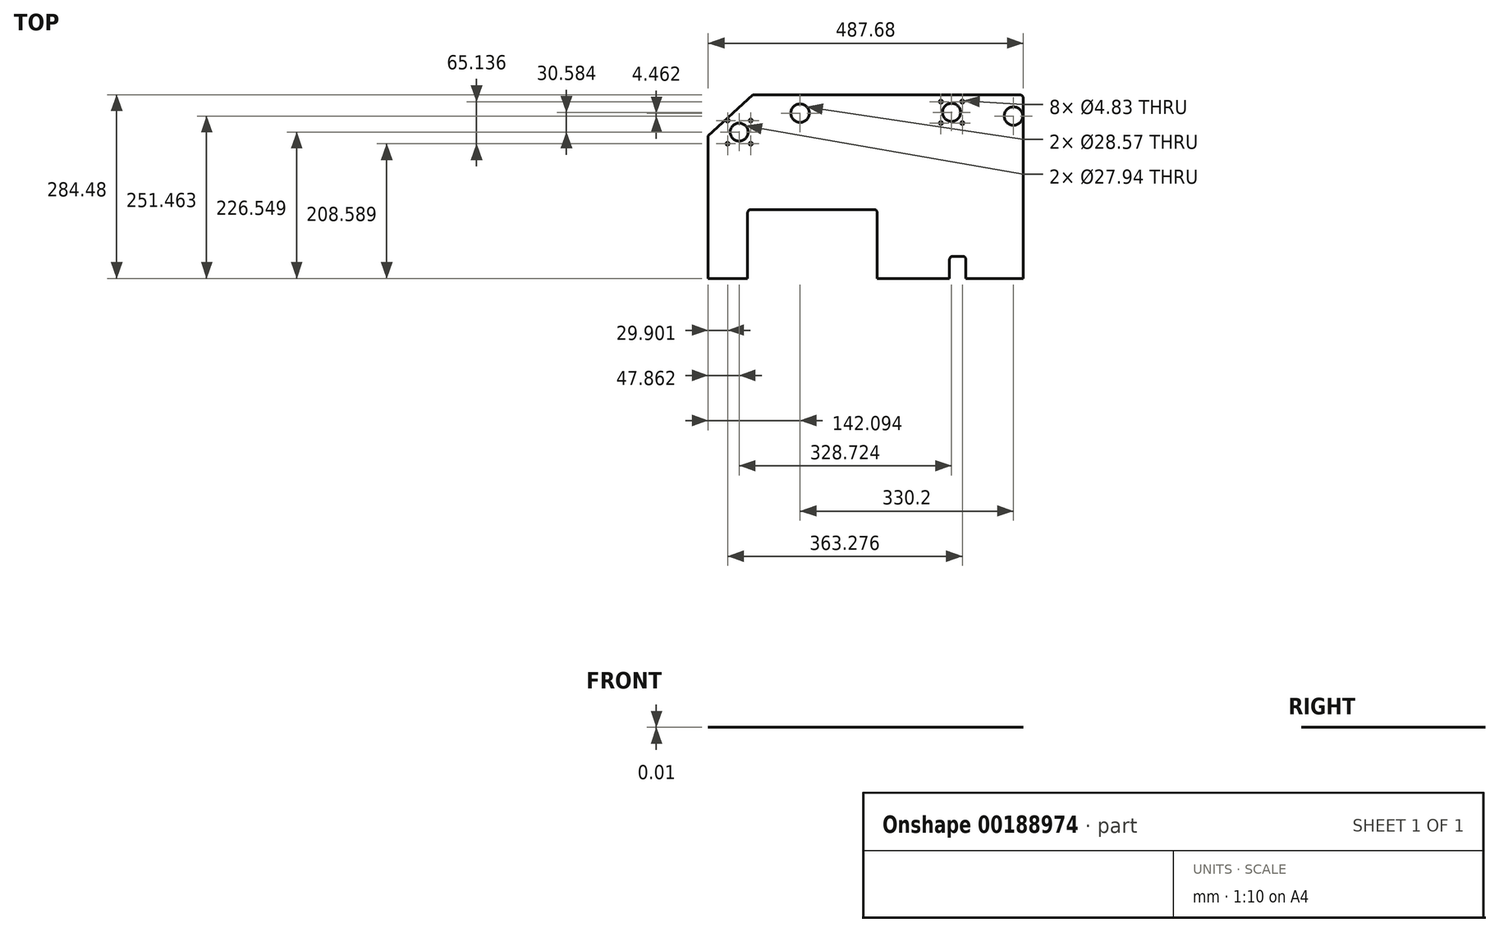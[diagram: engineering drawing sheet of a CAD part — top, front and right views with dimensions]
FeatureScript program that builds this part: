
annotation { "Feature Type Name" : "Feature", "Feature Type Description" : "" }
export const myFeature = defineFeature(function(context is Context, id is Id, definition is map)
    precondition{}
    {
        {
            var Q0;
            Q0=qCreatedBy(makeId("Top.planeOp"),FACE);
            var sketch = newSketch(context, id + "F0", { "sketchPlane" : qUnion([Q0])});
            skLineSegment(sketch, "E0.bottom", {"start": v(29.14, 37.07) * mm, "end": v(441.77, 37.07) * mm});
            skLineSegment(sketch, "E0.top", {"start": v(-39.56, -247.4) * mm, "end": v(21.4, -247.4) * mm});
            skLineSegment(sketch, "E0.left", {"start": v(-39.56, -26.6) * mm, "end": v(-39.56, -247.4) * mm});
            skLineSegment(sketch, "E0.right", {"start": v(448.12, 30.72) * mm, "end": v(448.12, -247.4) * mm});
            skLineSegment(sketch, "E1", {"start": v(-39.56, -26.6) * mm, "end": v(29.14, 37.07) * mm});
            skLineSegment(sketch, "E2.bottom", {"start": v(448.12, -247.4) * mm, "end": v(359.22, -247.4) * mm, "construction": true});
            skLineSegment(sketch, "E2.top", {"start": v(448.12, 37.07) * mm, "end": v(-39.56, 37.07) * mm, "construction": true});
            skLineSegment(sketch, "E2.left", {"start": v(448.12, -247.4) * mm, "end": v(448.12, 37.07) * mm, "construction": true});
            skLineSegment(sketch, "E2.right", {"start": v(-39.56, -247.4) * mm, "end": v(-39.56, 37.07) * mm, "construction": true});
            skCircle(sketch, "E3", {"center": v(432.73, 4.05) * mm, "radius": 14.29 * mm});
            skCircle(sketch, "E4", {"center": v(337.03, 9.72) * mm, "radius": 23.46 * mm, "construction": true});
            skLineSegment(sketch, "E5.bottom", {"start": v(320.44, 26.31) * mm, "end": v(353.62, 26.31) * mm, "construction": true});
            skLineSegment(sketch, "E5.top", {"start": v(320.44, -6.87) * mm, "end": v(353.62, -6.87) * mm, "construction": true});
            skLineSegment(sketch, "E5.left", {"start": v(320.44, 26.31) * mm, "end": v(320.44, -6.87) * mm, "construction": true});
            skLineSegment(sketch, "E5.right", {"start": v(353.62, 26.31) * mm, "end": v(353.62, -6.87) * mm, "construction": true});
            skCircle(sketch, "E6", {"center": v(320.44, 26.31) * mm, "radius": 2.41 * mm});
            skCircle(sketch, "E7", {"center": v(353.62, 26.31) * mm, "radius": 2.41 * mm});
            skCircle(sketch, "E8", {"center": v(353.62, -6.87) * mm, "radius": 2.41 * mm});
            skCircle(sketch, "E9", {"center": v(320.44, -6.87) * mm, "radius": 2.41 * mm});
            skCircle(sketch, "E10", {"center": v(337.03, 9.72) * mm, "radius": 13.97 * mm});
            skCircle(sketch, "E11", {"center": v(102.53, 8.52) * mm, "radius": 14.29 * mm});
            skLineSegment(sketch, "E12", {"start": v(333.82, -247.4) * mm, "end": v(333.82, -213.12) * mm});
            skLineSegment(sketch, "E13", {"start": v(333.82, -213.12) * mm, "end": v(359.22, -213.12) * mm});
            skLineSegment(sketch, "E14", {"start": v(359.22, -213.12) * mm, "end": v(359.22, -247.4) * mm});
            skLineSegment(sketch, "E15.trimOffspring", {"start": v(333.82, -247.4) * mm, "end": v(222.06, -247.4) * mm, "construction": true});
            skCircle(sketch, "E16", {"center": v(8.3, -20.86) * mm, "radius": 25.4 * mm, "construction": true});
            skLineSegment(sketch, "E17.bottom", {"start": v(-9.66, -2.9) * mm, "end": v(26.26, -2.9) * mm, "construction": true});
            skLineSegment(sketch, "E17.top", {"start": v(-9.66, -38.82) * mm, "end": v(26.26, -38.82) * mm, "construction": true});
            skLineSegment(sketch, "E17.left", {"start": v(-9.66, -2.9) * mm, "end": v(-9.66, -38.82) * mm, "construction": true});
            skLineSegment(sketch, "E17.right", {"start": v(26.26, -2.9) * mm, "end": v(26.26, -38.82) * mm, "construction": true});
            skCircle(sketch, "E18", {"center": v(-9.66, -2.9) * mm, "radius": 2.41 * mm});
            skCircle(sketch, "E19", {"center": v(26.26, -2.9) * mm, "radius": 2.41 * mm});
            skCircle(sketch, "E20", {"center": v(26.26, -38.82) * mm, "radius": 2.41 * mm});
            skCircle(sketch, "E21", {"center": v(-9.66, -38.82) * mm, "radius": 2.41 * mm});
            skCircle(sketch, "E22", {"center": v(8.3, -20.86) * mm, "radius": 13.97 * mm});
            skLineSegment(sketch, "E23.top", {"start": v(21.4, -140.73) * mm, "end": v(222.06, -140.73) * mm});
            skLineSegment(sketch, "E23.left", {"start": v(21.4, -247.4) * mm, "end": v(21.4, -140.73) * mm});
            skLineSegment(sketch, "E23.right", {"start": v(222.06, -247.4) * mm, "end": v(222.06, -140.73) * mm});
            skLineSegment(sketch, "E24.trimOffspring", {"start": v(21.4, -247.4) * mm, "end": v(-39.56, -247.4) * mm, "construction": true});
            skLineSegment(sketch, "E25.trimOffspring", {"start": v(222.06, -247.4) * mm, "end": v(448.12, -247.4) * mm});
            skLineSegment(sketch, "E26", {"start": v(8.3, -20.86) * mm, "end": v(102.53, 8.52) * mm, "construction": true});
            skCircle(sketch, "E27", {"center": v(102.53, 8.52) * mm, "radius": 50.8 * mm, "construction": true});
            skCircle(sketch, "E28", {"center": v(432.73, 4.05) * mm, "radius": 25.4 * mm, "construction": true});
            skPoint(sketch, "E29.visualSharp", {"position": v(448.12, 37.07) * mm});
            skArc(sketch, "E29.filletArc", {"start": v(448.12, 30.72) * mm, "mid": v(446.26, 35.21) * mm, "end": v(441.77, 37.07) * mm});
            skCircle(sketch, "E30", {"center": v(279.66, 10.81) * mm, "radius": 127 * mm, "construction": true});
            skSolve(sketch);
        }
        {
            var Q0;
            Q0=makeQuery(id+"F0.imprint","IMPRINT",FACE,{"disambiguationData":[TD([[makeQuery(id+"F0.imprint","IMPRINT",EDGE,{"derivedFrom":sQuery(id+"F0.wireOp",EDGE,"E0.bottom")}),-1.0]])]});
            extrude(context, id + "F1", {"entities" : qUnion([Q0]), "depth" : 1 / 101.6 * mm});
        }
        {
            var Q0;
            Q0=makeQuery(id+"F1.opExtrude","SWEPT_EDGE",EDGE,{"disambiguationData":[OSD([sQuery(id+"F0.wireOp",EDGE,"E23.top"),sQuery(id+"F0.wireOp",EDGE,"E23.left")])]});
            var Q1;
            Q1=makeQuery(id+"F1.opExtrude","SWEPT_EDGE",EDGE,{"disambiguationData":[OSD([sQuery(id+"F0.wireOp",EDGE,"E23.top"),sQuery(id+"F0.wireOp",EDGE,"E23.right")])]});
            var Q2;
            Q2=makeQuery(id+"F1.opExtrude","SWEPT_EDGE",EDGE,{"disambiguationData":[OSD([sQuery(id+"F0.wireOp",EDGE,"E12"),sQuery(id+"F0.wireOp",EDGE,"E13")])]});
            var Q3;
            Q3=makeQuery(id+"F1.opExtrude","SWEPT_EDGE",EDGE,{"disambiguationData":[OSD([sQuery(id+"F0.wireOp",EDGE,"E13"),sQuery(id+"F0.wireOp",EDGE,"E14")])]});
            fillet(context, id + "F2", {"entities" : qUnion([Q0, Q1, Q2, Q3]), "radius" : 5.08 * mm, "tangentPropagation" : true, "allowEdgeOverflow" : false});
        }
    });
